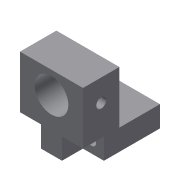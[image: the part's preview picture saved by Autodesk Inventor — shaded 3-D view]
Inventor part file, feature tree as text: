
AUTODESK INVENTOR PART (.ipt)
format: ipt  version: 2019.4 (Build 234330000, 330)  size: 148,992 bytes
history: native  units: mm
features: extrude x7, sketch x7, projected_geometry x4
ambient origin geometry x8: Origin, YZ Plane, XZ Plane, XY Plane, X Axis, Y Axis, Z Axis, Center Point
bodies: Solid1 (feature_tree)
feature tree (18):
  extrude  "Extrusion1"  Depth=6.0mm
  extrude  "Extrusion2"  Depth=2.5mm
  extrude  "Extrusion3"  Depth=2.8mm
  extrude  "Extrusion4"  Depth=3.5mm
  extrude  "Extrusion5"  Depth=22.0mm TaperAngle=0.0deg
  extrude  "Extrusion6"  Depth=15.0mm
  extrude  "Extrusion7"  Depth=9.6mm
  sketch  "Sketch1"  dims[d0=18.0mm d1=6.0mm]
  sketch  "Sketch2"  dims[d2=22.0mm d3=0.0mm d4=2.5mm]
  projected_geometry  "Projected Loop1"
  sketch  "Sketch3"  dims[d5=2.5mm d6=2.8mm]
  projected_geometry  "Projected Loop2"
  sketch  "Sketch4"  dims[d7=2.8mm d8=3.5mm]
  projected_geometry  "Projected Loop3"
  sketch  "Sketch5"  dims[d9=3.5mm d10=22.0mm d11=0.0mm]
  sketch  "Sketch6"  dims[d12=10.4mm d13=15.0mm]
  projected_geometry  "Projected Loop4"
  sketch  "Sketch7"  dims[d14=22.0mm d15=0.0mm d16=9.6mm d17=6.3mm d18=22.0mm d19=0.0mm d20=6.0mm d21=6.0mm d22=6.0mm d23=0.0mm d24=6.0mm d25=0.0mm d26=2.8mm d27=5.2mm d28=2.5mm d29=6.0mm d30=0.0mm]
